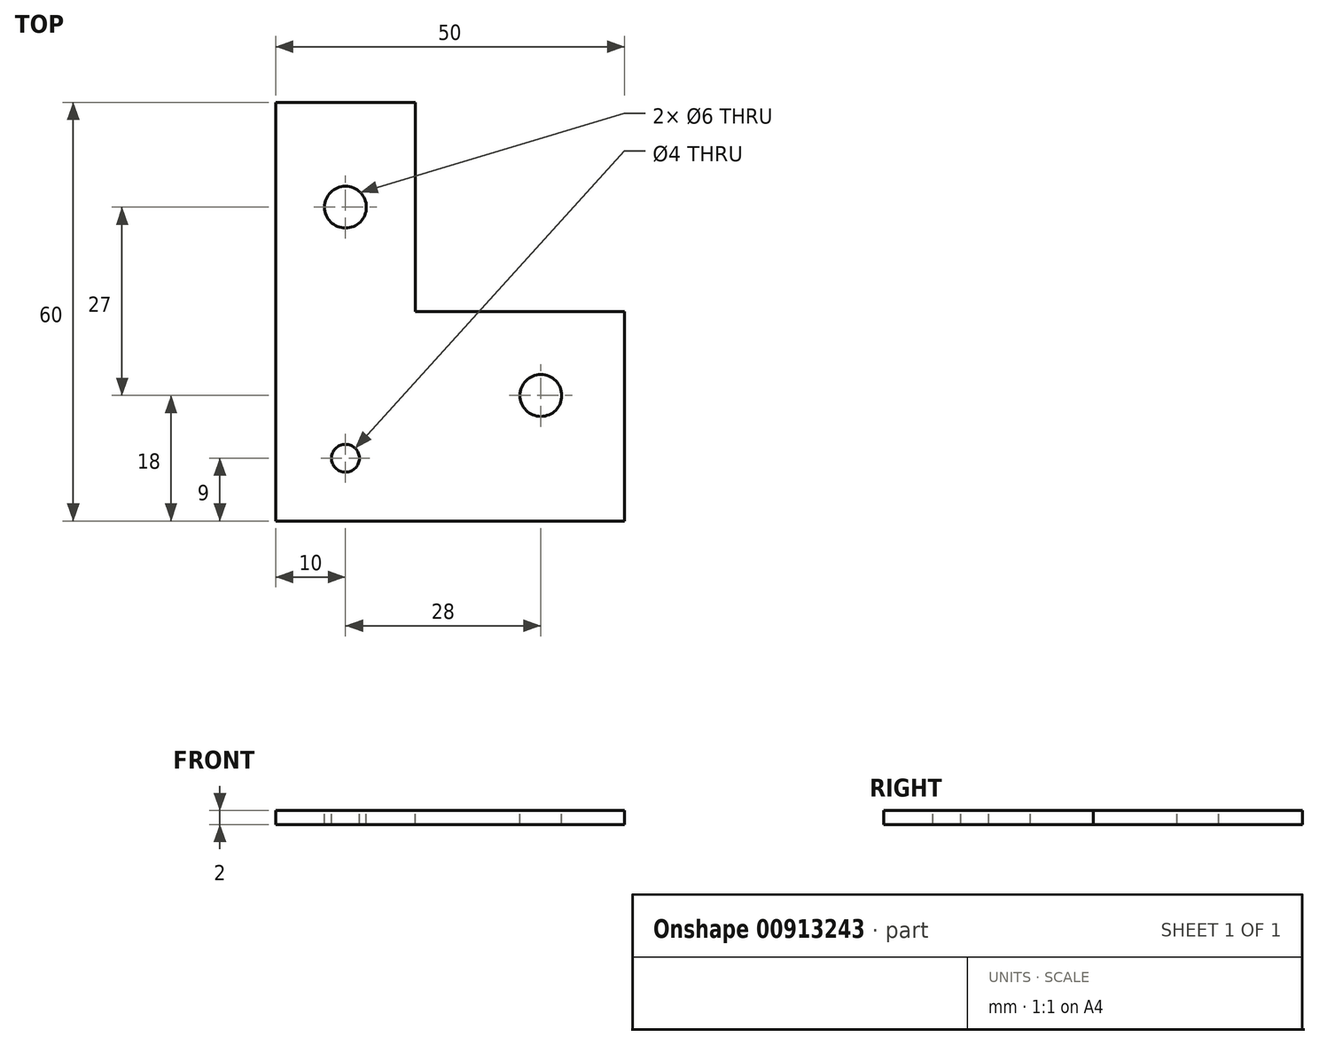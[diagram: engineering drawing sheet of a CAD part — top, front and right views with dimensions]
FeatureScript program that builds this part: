
annotation { "Feature Type Name" : "Feature", "Feature Type Description" : "" }
export const myFeature = defineFeature(function(context is Context, id is Id, definition is map)
    precondition{}
    {
        {
            var Q0;
            Q0=qCreatedBy(makeId("Top.planeOp"),FACE);
            var sketch = newSketch(context, id + "F0", { "sketchPlane" : qUnion([Q0])});
            skLineSegment(sketch, "E0.bottom", {"start": v(25, -30) * mm, "end": v(-25, -30) * mm});
            skLineSegment(sketch, "E0.top", {"start": v(25, 30) * mm, "end": v(-25, 30) * mm});
            skLineSegment(sketch, "E0.left", {"start": v(25, -30) * mm, "end": v(25, 30) * mm});
            skLineSegment(sketch, "E0.right", {"start": v(-25, -30) * mm, "end": v(-25, 30) * mm});
            skPoint(sketch, "E0.middle", {"position": v(0, 0) * mm});
            skLineSegment(sketch, "E1.bottom", {"start": v(25, 30) * mm, "end": v(-5, 30) * mm});
            skLineSegment(sketch, "E1.top", {"start": v(25, 0) * mm, "end": v(-5, 0) * mm});
            skLineSegment(sketch, "E1.left", {"start": v(25, 30) * mm, "end": v(25, 0) * mm});
            skLineSegment(sketch, "E1.right", {"start": v(-5, 30) * mm, "end": v(-5, 0) * mm});
            skCircle(sketch, "E2", {"center": v(-15, 15) * mm, "radius": 3 * mm});
            skCircle(sketch, "E3", {"center": v(13, -12) * mm, "radius": 3 * mm});
            skCircle(sketch, "E4", {"center": v(-15, -21) * mm, "radius": 2 * mm});
            skSolve(sketch);
        }
        {
            var Q0;
            Q0=makeQuery(id+"F0.imprint","IMPRINT",FACE,{"disambiguationData":[TD([[makeQuery(id+"F0.imprint","IMPRINT",EDGE,{"derivedFrom":sQuery(id+"F0.wireOp",EDGE,"E0.bottom")}),-1.0]])]});
            extrude(context, id + "F1", {"entities" : qUnion([Q0]), "oppositeDirection" : true, "depth" : 2 * mm, "offsetDistance" : 25 * mm});
        }
    });
